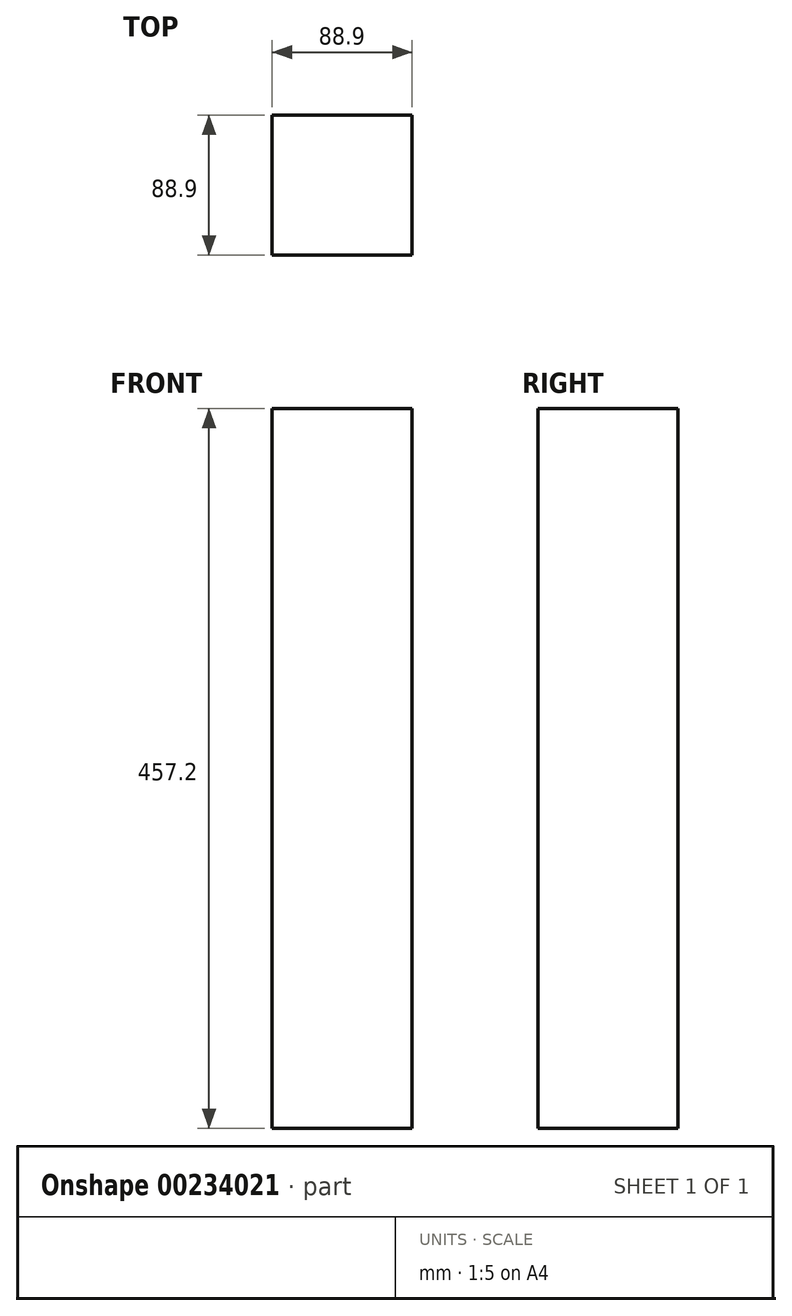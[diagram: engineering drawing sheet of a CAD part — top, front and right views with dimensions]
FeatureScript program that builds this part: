
annotation { "Feature Type Name" : "Feature", "Feature Type Description" : "" }
export const myFeature = defineFeature(function(context is Context, id is Id, definition is map)
    precondition{}
    {
        {
            var Q0;
            Q0=qCreatedBy(makeId("Top.planeOp"),FACE);
            var sketch = newSketch(context, id + "F0", { "sketchPlane" : qUnion([Q0])});
            skLineSegment(sketch, "E0.bottom", {"start": v(-42.77, 40.5) * mm, "end": v(46.13, 40.5) * mm});
            skLineSegment(sketch, "E0.top", {"start": v(-42.77, -48.4) * mm, "end": v(46.13, -48.4) * mm});
            skLineSegment(sketch, "E0.left", {"start": v(-42.77, 40.5) * mm, "end": v(-42.77, -48.4) * mm});
            skLineSegment(sketch, "E0.right", {"start": v(46.13, 40.5) * mm, "end": v(46.13, -48.4) * mm});
            skSolve(sketch);
        }
        {
            var Q0;
            Q0 = qSketchRegion(id + "F0", true);
            extrude(context, id + "F1", {"entities" : qUnion([Q0]), "depth" : 457.2 * mm});
        }
    });
